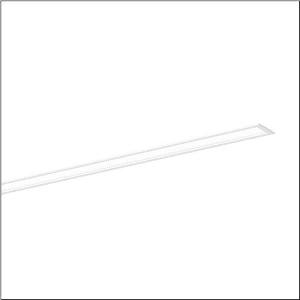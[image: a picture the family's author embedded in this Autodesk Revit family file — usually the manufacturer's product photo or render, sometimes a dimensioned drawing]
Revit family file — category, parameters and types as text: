
# Revit family: silica_r__21_51mx13tctaw_ab10
name_source: partatom
category: Lighting Fixtures
units: mm (PartAtom-declared; Revit-internal decimal feet)

## family parameters
Cut with Voids When Loaded = No
Host = Face
Light Source = No
Part Type = Normal
Room Calculation Point = No
Round Connector Dimension = Use Diameter
Shared = No

## types (1)
- --- (1 x LED, 8070 lm, 81.1 W, 6500K)
    Apparent Load = 81 VA
    CIE Flux Codes = 78 96 99 100 100
    Color Rendering = 80
    Color Temperature = 6500K
    Default Elevation = 1800 mm
    Description = Silica® 21, office luminaire, primary optical cover: prismatic diffuser, of PMMA, CAT 2 (L<= 3000cd/m²), light emission: direct distribution, primary light characteristic: symmetric, installation type: recessed, LED, rated luminous flux: 8.070lm, luminous efficacy: 95lm/W, light colour: 8tw, colour temperature: 2700..6500K, with terminal, 3+2-pole, max. 2.5mm², mains connection: 220..240V, AC, 50/60Hz, rated input power: 85.1W, luminaire housing, of aluminium, traffic white (RAL 9016), length: 3.028mm, width: 79mm, height: 53mm, protection rating (complete): IP20, insulation class (complete): insulation class I (protective earthing), certification: CE, permissible operating ambient temperature: 0..+35°C, standard: EN 50419, packaging unit: 1 piece
    Height = 0 mm  [stored 0 ft]
    Lamp = 1 x LED
    Lamp Light Flux = 8070 lm
    Lamp Power = 81.1 W
    Lamp count = 1
    Length = 3027 mm
    Luminous efficacy = 100 lm/W
    Manufacturer = Siteco
    ModVariant = No
    Model = 51MX13TCTAW
    Mounting Place = Ceiling
    Mounting Type = Recessed
    Number of Poles = 1
    OnlyDefault = Yes
    Power Factor = 1
    Product Name = Silica® 21
    Product group = office luminaire | ceiling recessed
    ProductGroupID = 401
    Protection Class = Protection class I
    Protection Degree = IP 20
    RLX_Detail_Level = 1
    RLX_Emergency_Light_Flux = 0 lm
    RLX_Emergency_Type = 0
    RLX_Emergency_Type_DB = No
    RlxData = <blob elided: 13041 chars, md5=1e2dd826>
    Socket = socket
    Standby Power = 0 W
    System Light Flux = 8070 lm
    System Power = 81 W
    Type Comments = individual setting
    Type Image = l_1313611.jpg
    URL = http://relux.com
    VarID = @adj_089211
    Voltage = 0 V
    Weight = 0.00 kg
    Width = 79 mm

note: [stored X ft] marks values corroborated as IEEE doubles in the binary element streams (Revit-internal decimal feet)

## geometry (parser evidence)
native form markers: Sweep x10
no freeform markers — native parametric forms only
